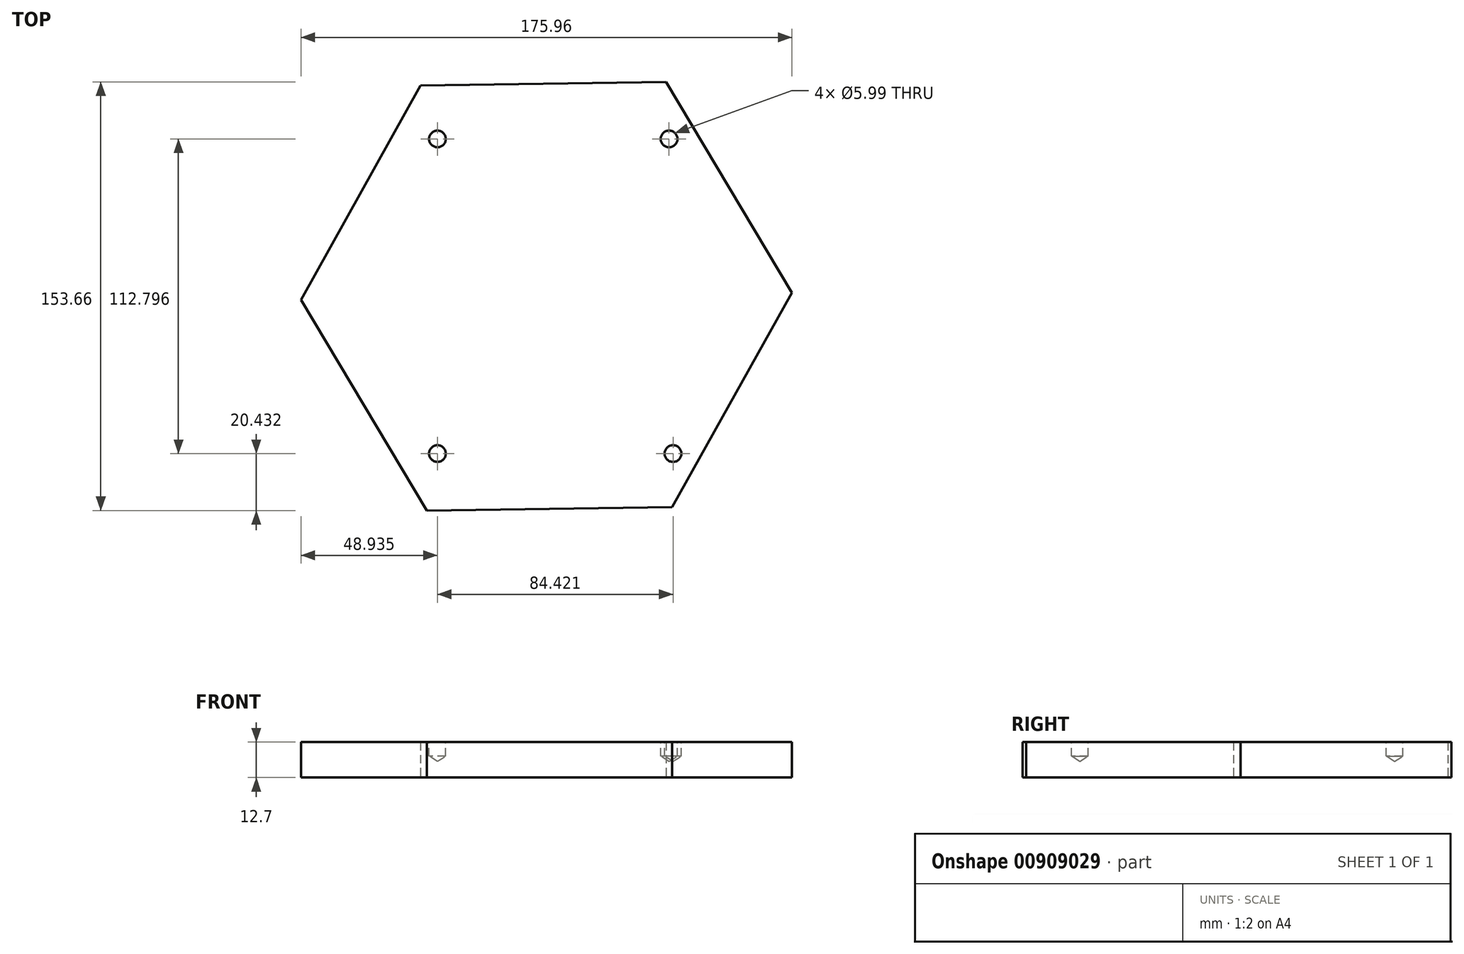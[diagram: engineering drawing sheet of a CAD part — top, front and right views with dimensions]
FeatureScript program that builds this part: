
annotation { "Feature Type Name" : "Feature", "Feature Type Description" : "" }
export const myFeature = defineFeature(function(context is Context, id is Id, definition is map)
    precondition{}
    {
        {
            var Q0;
            Q0=qCreatedBy(makeId("Top.planeOp"),FACE);
            var sketch = newSketch(context, id + "F0", { "sketchPlane" : qUnion([Q0])});
            skCircle(sketch, "E0.cCircle", {"center": v(0, 0) * mm, "radius": 76.2 * mm, "construction": true});
            skLineSegment(sketch, "E0.0", {"start": v(87.98, 1.27) * mm, "end": v(45.1, -75.56) * mm});
            skLineSegment(sketch, "E0.1", {"start": v(45.1, -75.56) * mm, "end": v(-42.89, -76.83) * mm});
            skLineSegment(sketch, "E0.2", {"start": v(-42.89, -76.83) * mm, "end": v(-87.98, -1.27) * mm});
            skLineSegment(sketch, "E0.3", {"start": v(-87.98, -1.27) * mm, "end": v(-45.1, 75.56) * mm});
            skLineSegment(sketch, "E0.4", {"start": v(-45.1, 75.56) * mm, "end": v(42.89, 76.83) * mm});
            skLineSegment(sketch, "E0.5", {"start": v(42.89, 76.83) * mm, "end": v(87.98, 1.27) * mm});
            skPoint(sketch, "E0.0.midPoint", {"position": v(66.53, -37.14) * mm});
            skSolve(sketch);
        }
        {
            var Q0;
            Q0=makeQuery(id+"F0.imprint","IMPRINT",FACE,{"disambiguationData":[TD([[makeQuery(id+"F0.imprint","IMPRINT",EDGE,{"derivedFrom":sQuery(id+"F0.wireOp",EDGE,"E0.0")}),-1.0]])]});
            extrude(context, id + "F1", {"entities" : qUnion([Q0]), "depth" : 12.7 * mm, "offsetDistance" : 25.4 * mm});
        }
        {
            var Q0;
            Q0=makeQuery(id+"F1.opExtrude","CAP_FACE",FACE,{"disambiguationData":[OSD([sQuery(id+"F0.wireOp",EDGE,"E0.0"),sQuery(id+"F0.wireOp",EDGE,"E0.1"),sQuery(id+"F0.wireOp",EDGE,"E0.2"),sQuery(id+"F0.wireOp",EDGE,"E0.3"),sQuery(id+"F0.wireOp",EDGE,"E0.4"),sQuery(id+"F0.wireOp",EDGE,"E0.5")])],"isStart":false});
            var sketch = newSketch(context, id + "F2", { "sketchPlane" : qUnion([Q0])});
            skPoint(sketch, "E1", {"position": v(-39.04, 56.4) * mm});
            skPoint(sketch, "E2", {"position": v(-39.04, -56.4) * mm});
            skPoint(sketch, "E3", {"position": v(45.38, -56.4) * mm});
            skPoint(sketch, "E4", {"position": v(43.97, 56.4) * mm});
            skSolve(sketch);
        }
        {
            var Q0;
            Q0=sQuery(id+"F2.wireOp",VERTEX,"E1");
            var Q1;
            Q1=sQuery(id+"F2.wireOp",VERTEX,"E4");
            var Q2;
            Q2=sQuery(id+"F2.wireOp",VERTEX,"E2");
            var Q3;
            Q3=sQuery(id+"F2.wireOp",VERTEX,"E3");
            var Q4;
            Q4=makeQuery(id+"F1.opExtrude","SWEPT_BODY",BODY,{"disambiguationData":[OSD([sQuery(id+"F0.wireOp",EDGE,"E0.0"),sQuery(id+"F0.wireOp",EDGE,"E0.1"),sQuery(id+"F0.wireOp",EDGE,"E0.2"),sQuery(id+"F0.wireOp",EDGE,"E0.3"),sQuery(id+"F0.wireOp",EDGE,"E0.4"),sQuery(id+"F0.wireOp",EDGE,"E0.5")])]});
            hole(context, id + "F3", {"style" : HoleStyle.SIMPLE, "endStyle" : HoleEndStyle.BLIND, "holeDiameter" : 6 * mm, "majorDiameter" : 6.35 * mm, "holeDepth" : 5.08 * mm, "isTappedThrough" : true, "tappedDepth" : 12.7 * mm, "tapClearance" : 3, "startFromSketch" : true, "locations" : qUnion([Q0, Q1, Q2, Q3]), "scope" : qUnion([Q4])});
        }
    });
